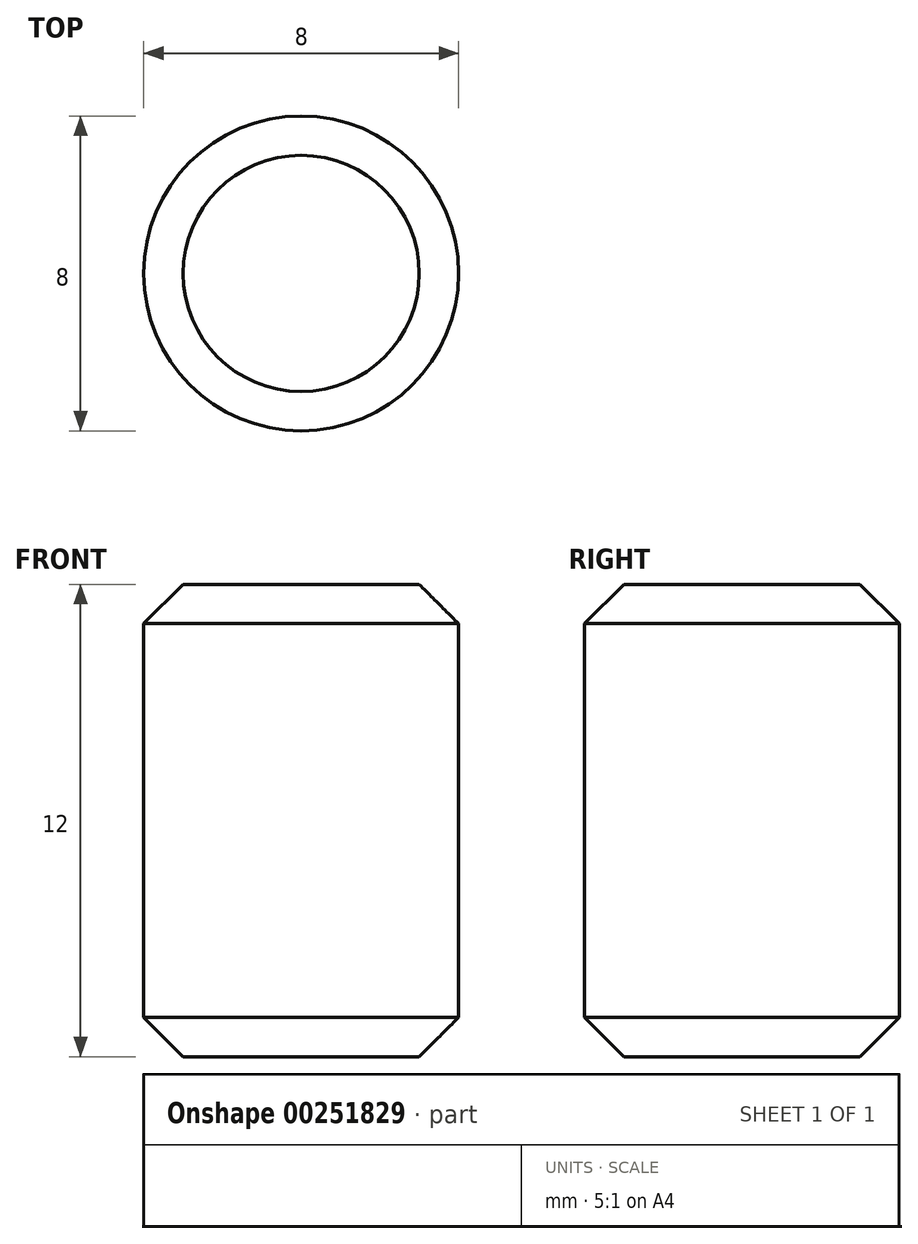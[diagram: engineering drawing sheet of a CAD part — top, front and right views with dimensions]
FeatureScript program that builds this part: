
annotation { "Feature Type Name" : "Feature", "Feature Type Description" : "" }
export const myFeature = defineFeature(function(context is Context, id is Id, definition is map)
    precondition{}
    {
        {
            var Q0;
            Q0=qCreatedBy(makeId("Top.planeOp"),FACE);
            var sketch = newSketch(context, id + "F0", { "sketchPlane" : qUnion([Q0])});
            skCircle(sketch, "E0", {"center": v(0, 0) * mm, "radius": 4 * mm});
            skSolve(sketch);
        }
        {
            var Q0;
            Q0=makeQuery(id+"F0.imprint","IMPRINT",FACE,{"disambiguationData":[TD([[makeQuery(id+"F0.imprint","IMPRINT",EDGE,{"derivedFrom":sQuery(id+"F0.wireOp",EDGE,"E0")}),1.0]])]});
            extrude(context, id + "F1", {"entities" : qUnion([Q0]), "depth" : 12 * mm});
        }
        {
            var Q0;
            Q0=makeQuery(id+"F1.opExtrude","CAP_FACE",FACE,{"disambiguationData":[OSD([sQuery(id+"F0.wireOp",EDGE,"E0")])],"isStart":false});
            var Q1;
            Q1=makeQuery(id+"F1.opExtrude","CAP_EDGE",EDGE,{"disambiguationData":[OSD([sQuery(id+"F0.wireOp",EDGE,"E0")])],"isStart":true});
            chamfer(context, id + "F2", {"entities" : qUnion([Q0, Q1]), "chamferType" : ChamferType.OFFSET_ANGLE, "width" : 1 * mm, "oppositeDirection" : false, "angle" : 45 * degree, "tangentPropagation" : true});
        }
    });
